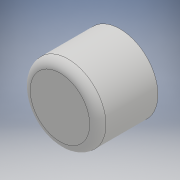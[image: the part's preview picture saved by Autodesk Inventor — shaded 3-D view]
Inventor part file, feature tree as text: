
AUTODESK INVENTOR PART (.ipt)
format: ipt  version: 2017 (Build 210142000, 142)  size: 120,320 bytes
history: native  units: mm
features: extrude x2, sketch x2, fillet x1
ambient origin geometry x8: Origin, YZ Plane, XZ Plane, XY Plane, X Axis, Y Axis, Z Axis, Center Point
bodies: Body1 (feature_tree)
feature tree (5):
  extrude  "Extrusion4"  Depth=3.0mm
  extrude  "Extrusion5"  Depth=3.0mm TaperAngle=0.0deg
  fillet  "Fillet2"  Radius=3.0mm
  sketch  "Sketch5"  dims[d11=22.0mm d12=3.0mm]
  sketch  "Sketch6"  dims[d13=19.225mm d14=0.0mm d15=3.0mm d16=0.0mm d17=3.0mm]
